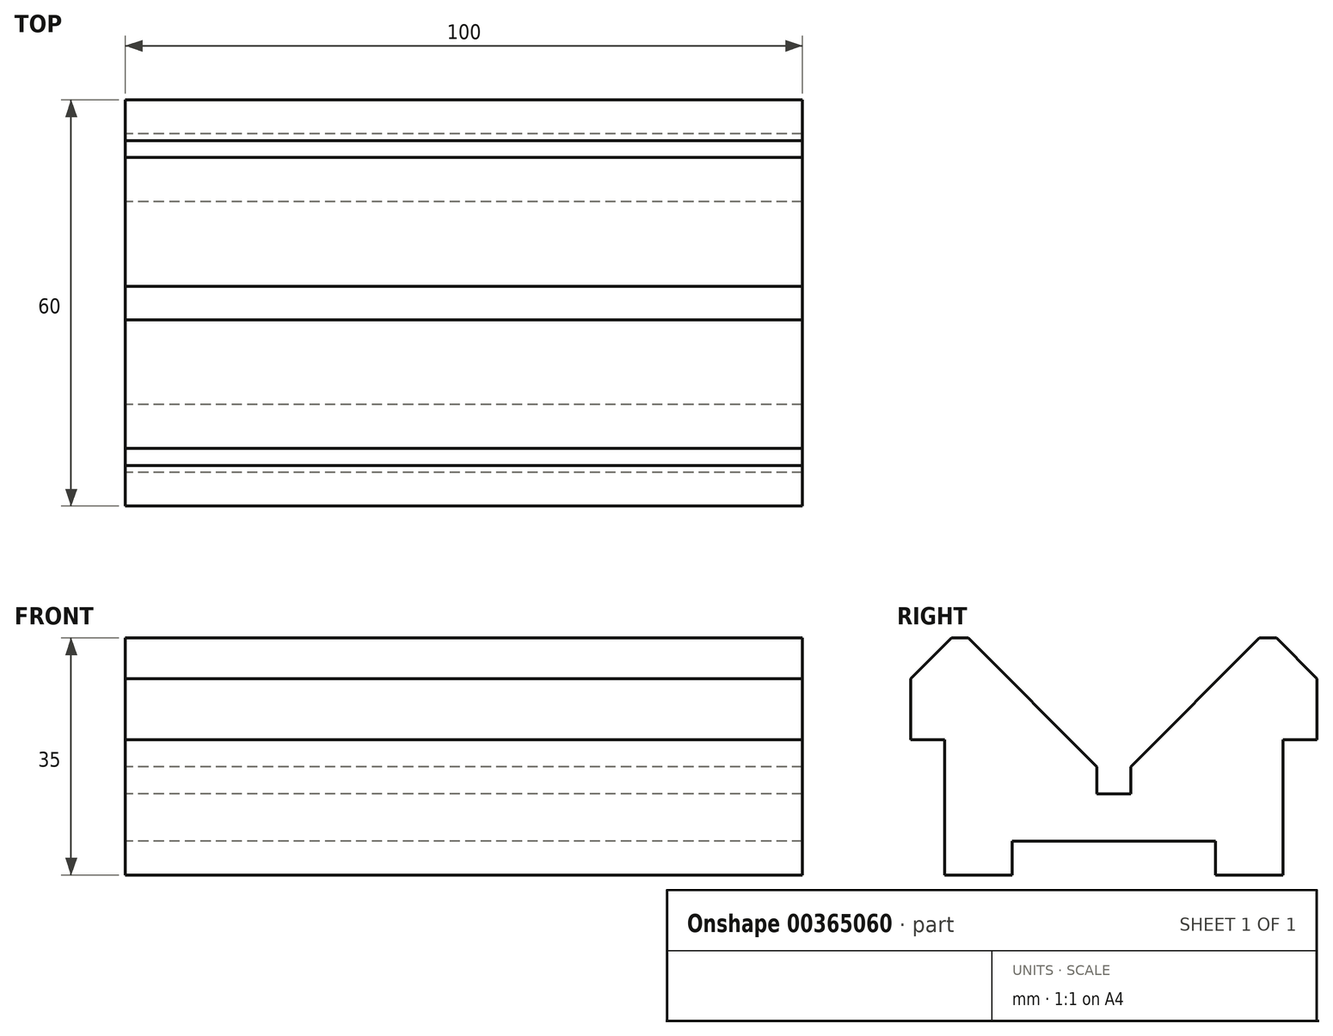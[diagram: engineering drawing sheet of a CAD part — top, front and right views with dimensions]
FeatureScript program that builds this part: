
annotation { "Feature Type Name" : "Feature", "Feature Type Description" : "" }
export const myFeature = defineFeature(function(context is Context, id is Id, definition is map)
    precondition{}
    {
        {
            var Q0;
            Q0=qCreatedBy(makeId("Right.planeOp"),FACE);
            var sketch = newSketch(context, id + "F0", { "sketchPlane" : qUnion([Q0])});
            skLineSegment(sketch, "E0", {"start": v(0, 0) * mm, "end": v(-5, 0) * mm});
            skLineSegment(sketch, "E1", {"start": v(-5, 0) * mm, "end": v(0, 0) * mm});
            skLineSegment(sketch, "E2", {"start": v(19, 23) * mm, "end": v(21.5, 23) * mm});
            skLineSegment(sketch, "E3", {"start": v(21.5, 23) * mm, "end": v(27.5, 17) * mm});
            skLineSegment(sketch, "E4", {"start": v(27.5, 17) * mm, "end": v(27.5, 8) * mm});
            skLineSegment(sketch, "E5", {"start": v(27.5, 8) * mm, "end": v(22.5, 8) * mm});
            skLineSegment(sketch, "E6", {"start": v(22.5, 8) * mm, "end": v(22.5, -12) * mm});
            skLineSegment(sketch, "E7", {"start": v(22.5, -12) * mm, "end": v(12.5, -12) * mm});
            skLineSegment(sketch, "E8", {"start": v(12.5, -12) * mm, "end": v(12.5, -7) * mm});
            skLineSegment(sketch, "E9", {"start": v(12.5, -7) * mm, "end": v(-17.5, -7) * mm});
            skLineSegment(sketch, "E10", {"start": v(-17.5, -7) * mm, "end": v(-17.5, -12) * mm});
            skLineSegment(sketch, "E11", {"start": v(-17.5, -12) * mm, "end": v(-27.5, -12) * mm});
            skLineSegment(sketch, "E12", {"start": v(-27.5, -12) * mm, "end": v(-27.5, 8) * mm});
            skLineSegment(sketch, "E13", {"start": v(-27.5, 8) * mm, "end": v(-32.5, 8) * mm});
            skLineSegment(sketch, "E14", {"start": v(-32.5, 8) * mm, "end": v(-32.5, 17) * mm});
            skLineSegment(sketch, "E15", {"start": v(-32.5, 17) * mm, "end": v(-26.5, 23) * mm});
            skLineSegment(sketch, "E16", {"start": v(-26.5, 23) * mm, "end": v(-24, 23) * mm});
            skLineSegment(sketch, "E17", {"start": v(-24, 23) * mm, "end": v(-5, 4) * mm});
            skLineSegment(sketch, "E18", {"start": v(-5, 4) * mm, "end": v(-5, 0) * mm});
            skLineSegment(sketch, "E19", {"start": v(0, 0) * mm, "end": v(0, 4) * mm});
            skLineSegment(sketch, "E20", {"start": v(0, 4) * mm, "end": v(19, 23) * mm});
            skSolve(sketch);
        }
        {
            var Q0;
            Q0 = qSketchRegion(id + "F0", true);
            extrude(context, id + "F1", {"entities" : qUnion([Q0]), "depth" : 100 * mm});
        }
    });
